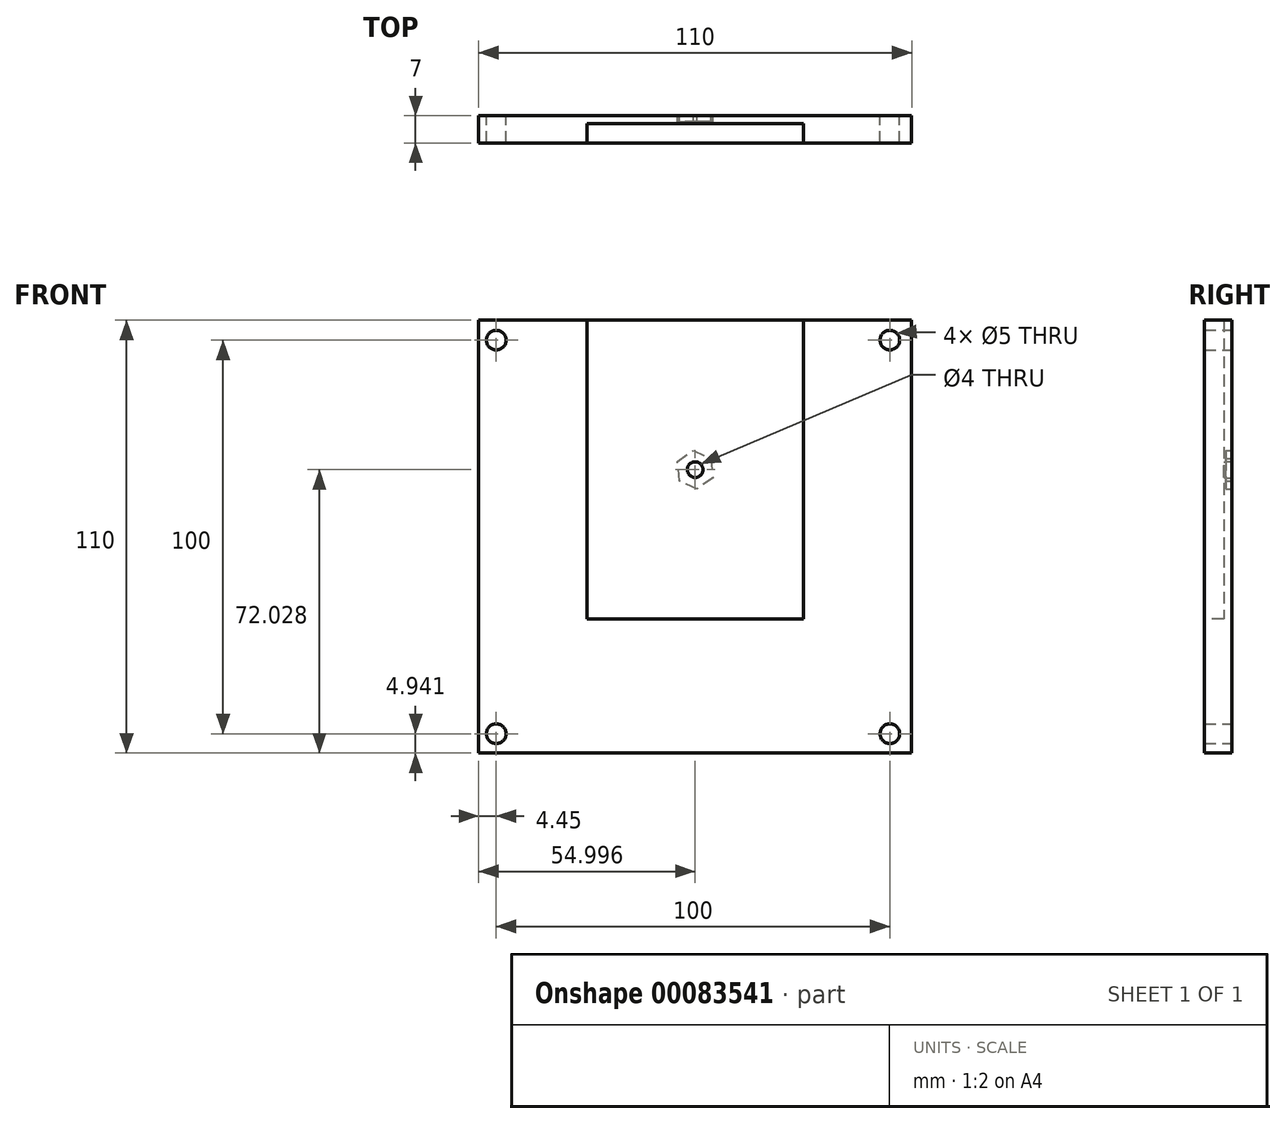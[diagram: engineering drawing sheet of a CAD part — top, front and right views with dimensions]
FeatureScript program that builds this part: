
annotation { "Feature Type Name" : "Feature", "Feature Type Description" : "" }
export const myFeature = defineFeature(function(context is Context, id is Id, definition is map)
    precondition{}
    {
        {
            var Q0;
            Q0=qCreatedBy(makeId("Front.planeOp"),FACE);
            var sketch = newSketch(context, id + "F0", { "sketchPlane" : qUnion([Q0])});
            skLineSegment(sketch, "E0.bottom", {"start": v(-61.36, 75.36) * mm, "end": v(48.64, 75.36) * mm});
            skLineSegment(sketch, "E0.top", {"start": v(-61.36, -34.64) * mm, "end": v(48.64, -34.64) * mm});
            skLineSegment(sketch, "E0.left", {"start": v(-61.36, 75.36) * mm, "end": v(-61.36, -34.64) * mm});
            skLineSegment(sketch, "E0.right", {"start": v(48.64, 75.36) * mm, "end": v(48.64, -34.64) * mm});
            skCircle(sketch, "E1", {"center": v(-56.9, 70.3) * mm, "radius": 2.5 * mm});
            skCircle(sketch, "E2", {"center": v(43.1, 70.3) * mm, "radius": 2.5 * mm});
            skCircle(sketch, "E3", {"center": v(43.1, -29.7) * mm, "radius": 2.5 * mm});
            skCircle(sketch, "E4", {"center": v(-56.9, -29.7) * mm, "radius": 2.5 * mm});
            skLineSegment(sketch, "E5", {"start": v(-6.36, 75.36) * mm, "end": v(-6.36, -0.59) * mm});
            skLineSegment(sketch, "E6.bottom", {"start": v(-33.86, 75.36) * mm, "end": v(21.14, 75.36) * mm});
            skLineSegment(sketch, "E6.top", {"start": v(-33.86, -0.59) * mm, "end": v(21.14, -0.59) * mm});
            skLineSegment(sketch, "E6.left", {"start": v(-33.86, 75.36) * mm, "end": v(-33.86, -0.59) * mm});
            skLineSegment(sketch, "E6.right", {"start": v(21.14, 75.36) * mm, "end": v(21.14, -0.59) * mm});
            skPoint(sketch, "E6.middle", {"position": v(-6.36, 37.39) * mm});
            skPoint(sketch, "E7.start.orphan", {"position": v(-58.86, 75.36) * mm});
            skPoint(sketch, "E8.orphan", {"position": v(-61.36, 72.86) * mm});
            skPoint(sketch, "E9.start.orphan", {"position": v(46.14, 75.36) * mm});
            skPoint(sketch, "E10.orphan", {"position": v(-61.36, -32.14) * mm});
            skLineSegment(sketch, "E11", {"start": v(-61.36, 20.36) * mm, "end": v(48.64, 20.36) * mm});
            skPoint(sketch, "E11.endSnap0", {"position": v(48.64, 20.36) * mm});
            skCircle(sketch, "E12.cCircle", {"center": v(-6.36, 37.39) * mm, "radius": 4.27 * mm, "construction": true});
            skLineSegment(sketch, "E12.0", {"start": v(-1.89, 35.31) * mm, "end": v(-5.92, 32.47) * mm});
            skLineSegment(sketch, "E12.1", {"start": v(-5.92, 32.47) * mm, "end": v(-10.4, 34.55) * mm});
            skLineSegment(sketch, "E12.2", {"start": v(-10.4, 34.55) * mm, "end": v(-10.84, 39.47) * mm});
            skLineSegment(sketch, "E12.3", {"start": v(-10.84, 39.47) * mm, "end": v(-6.8, 42.3) * mm});
            skLineSegment(sketch, "E12.4", {"start": v(-6.8, 42.3) * mm, "end": v(-2.33, 40.23) * mm});
            skLineSegment(sketch, "E12.5", {"start": v(-2.33, 40.23) * mm, "end": v(-1.89, 35.31) * mm});
            skPoint(sketch, "E12.0.midPoint", {"position": v(-3.9, 33.9) * mm});
            skCircle(sketch, "E13", {"center": v(-6.36, 37.39) * mm, "radius": 2 * mm});
            skSolve(sketch);
        }
        {
            var Q0;
            Q0=makeQuery(id+"F0.imprint","IMPRINT",FACE,{"disambiguationData":[TD([[makeQuery(id+"F0.imprint","IMPRINT",EDGE,{"derivedFrom":sQuery(id+"F0.wireOp",EDGE,"E1")}),-1.0]])]});
            var Q1;
            {var subQ10=sQuery(id+"F0.wireOp",EDGE,"E0.top");Q1=makeQuery(id+"F0.imprint","IMPRINT",FACE,{"disambiguationData":[TD([[makeQuery(id+"F0.imprint","IMPRINT",EDGE,{"derivedFrom":subQ10}),1.0]])]});}
            var Q2;
            Q2=makeQuery(id+"F0.imprint","IMPRINT",FACE,{"disambiguationData":[TD([[makeQuery(id+"F0.imprint","IMPRINT",EDGE,{"derivedFrom":sQuery(id+"F0.wireOp",EDGE,"E2")}),-1.0]])]});
            var Q3;
            {var subQ5=sQuery(id+"F0.wireOp",EDGE,"E12.2");Q3=makeQuery(id+"F0.imprint","IMPRINT",FACE,{"disambiguationData":[TD([[makeQuery(id+"F0.imprint","IMPRINT",EDGE,{"derivedFrom":subQ5}),1.0]])]});}
            var Q4;
            {var subQ5=sQuery(id+"F0.wireOp",EDGE,"E12.0");Q4=makeQuery(id+"F0.imprint","IMPRINT",FACE,{"disambiguationData":[TD([[makeQuery(id+"F0.imprint","IMPRINT",EDGE,{"derivedFrom":subQ5}),1.0]])]});}
            var Q5;
            {var subQ0=sQuery(id+"F0.wireOp",EDGE,"E6.top");var subQ1=sQuery(id+"F0.wireOp",EDGE,"E5");var subQ2=makeQuery(id+"F0.imprint","INTERSECT",VERTEX,{"derivedFrom":[subQ1,subQ0]});Q5=makeQuery(id+"F0.imprint","IMPRINT",FACE,{"disambiguationData":[TD([[makeQuery(id+"F0.imprint","IMPRINT",EDGE,{"disambiguationData":[TD([[subQ2,1.0]])],"derivedFrom":subQ1}),-1.0]])]});}
            var Q6;
            {var subQ0=sQuery(id+"F0.wireOp",EDGE,"E6.top");var subQ1=sQuery(id+"F0.wireOp",EDGE,"E5");var subQ2=makeQuery(id+"F0.imprint","INTERSECT",VERTEX,{"derivedFrom":[subQ1,subQ0]});Q6=makeQuery(id+"F0.imprint","IMPRINT",FACE,{"disambiguationData":[TD([[makeQuery(id+"F0.imprint","IMPRINT",EDGE,{"disambiguationData":[TD([[subQ2,1.0]])],"derivedFrom":subQ1}),1.0]])]});}
            var Q7;
            {var subQ1=sQuery(id+"F0.wireOp",EDGE,"E12.0");Q7=makeQuery(id+"F0.imprint","IMPRINT",FACE,{"disambiguationData":[TD([[makeQuery(id+"F0.imprint","IMPRINT",EDGE,{"derivedFrom":subQ1}),-1.0]])]});}
            var Q8;
            {var subQ0=sQuery(id+"F0.wireOp",EDGE,"E12.2");Q8=makeQuery(id+"F0.imprint","IMPRINT",FACE,{"disambiguationData":[TD([[makeQuery(id+"F0.imprint","IMPRINT",EDGE,{"derivedFrom":subQ0}),-1.0]])]});}
            extrude(context, id + "F1", {"entities" : qUnion([Q0, Q1, Q2, Q3, Q4, Q5, Q6, Q7, Q8]), "depth" : 7 * mm});
        }
        {
            var Q0;
            Q0=makeQuery(id+"F1.opExtrude","CAP_FACE",FACE,{"disambiguationData":[OSD([sQuery(id+"F0.wireOp",EDGE,"E0.bottom"),sQuery(id+"F0.wireOp",EDGE,"E0.top"),sQuery(id+"F0.wireOp",EDGE,"E0.left"),sQuery(id+"F0.wireOp",EDGE,"E0.right"),sQuery(id+"F0.wireOp",EDGE,"E1"),sQuery(id+"F0.wireOp",EDGE,"E2"),sQuery(id+"F0.wireOp",EDGE,"E3"),sQuery(id+"F0.wireOp",EDGE,"E4"),sQuery(id+"F0.wireOp",EDGE,"E6.bottom")])],"isStart":false});
            var sketch = newSketch(context, id + "F2", { "sketchPlane" : qUnion([Q0])});
            skLineSegment(sketch, "E14.0", {"start": v(-33.86, 75.36) * mm, "end": v(-33.86, -0.59) * mm});
            skLineSegment(sketch, "E14.1", {"start": v(21.14, 75.36) * mm, "end": v(21.14, -0.59) * mm});
            skLineSegment(sketch, "E14.2", {"start": v(-33.86, 75.36) * mm, "end": v(21.14, 75.36) * mm});
            skLineSegment(sketch, "E14.3", {"start": v(-33.86, -0.59) * mm, "end": v(21.14, -0.59) * mm});
            skSolve(sketch);
        }
        {
            var Q0;
            Q0 = qSketchRegion(id + "F2", true);
            extrude(context, id + "F3", {"entities" : qUnion([Q0]), "operationType" : NewBodyOperationType.REMOVE, "oppositeDirection" : true, "depth" : 5 * mm});
        }
        {
            var Q0;
            {var subQ1=sQuery(id+"F0.wireOp",EDGE,"E12.0");Q0=makeQuery(id+"F0.imprint","IMPRINT",FACE,{"disambiguationData":[TD([[makeQuery(id+"F0.imprint","IMPRINT",EDGE,{"derivedFrom":subQ1}),-1.0]])]});}
            var Q1;
            {var subQ0=sQuery(id+"F0.wireOp",EDGE,"E12.2");Q1=makeQuery(id+"F0.imprint","IMPRINT",FACE,{"disambiguationData":[TD([[makeQuery(id+"F0.imprint","IMPRINT",EDGE,{"derivedFrom":subQ0}),-1.0]])]});}
            var Q2;
            Q2=sQuery(id+"F0.wireOp",EDGE,"E12.4");
            var Q3;
            Q3=sQuery(id+"F0.wireOp",EDGE,"E12.3");
            var Q4;
            Q4=sQuery(id+"F0.wireOp",EDGE,"E12.2");
            var Q5;
            Q5=sQuery(id+"F0.wireOp",EDGE,"E12.1");
            var Q6;
            Q6=sQuery(id+"F0.wireOp",EDGE,"E12.0");
            var Q7;
            Q7=sQuery(id+"F0.wireOp",EDGE,"E12.5");
            extrude(context, id + "F4", {"entities" : qUnion([Q0, Q1]), "operationType" : NewBodyOperationType.REMOVE, "surfaceEntities" : qUnion([Q2, Q3, Q4, Q5, Q6, Q7]), "depth" : 1.5 * mm});
        }
    });
